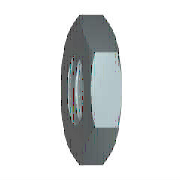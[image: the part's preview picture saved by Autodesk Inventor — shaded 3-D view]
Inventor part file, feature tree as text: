
AUTODESK INVENTOR PART (.ipt)
format: ipt  version: 2020 (Build 240168000, 168)  size: 167,424 bytes
history: native  units: mm (DEFAULTED — no unit token found)
features: sketch x3, chamfer x1, hole x1, other x1, plane x1
ambient origin geometry x7: Origin, YZ Plane, XZ Plane, X Axis, Y Axis, Z Axis, Center Point
bodies: Solid1 (feature_tree), Body (feature_tree)
feature tree (7):
  chamfer  "Chamfer1"  Angle=30.0deg  [1 undecoded]
  hole  "Thread"  [1 undecoded]
  other  "Work Axis1"
  plane  "Work Plane1"
  sketch  "Sketch1"  dims[d0=9.237604mm]
  sketch  "Sketch2"  dims[d1=2.7mm]
  sketch  "Sketch3"  dims[d2=0.0mm d3=30.0deg d4=30.0deg d5=6.9mm d6=6.9mm d7=90.0deg d25=4.134mm d26=6.0mm d27=4.0mm d28=2.0mm d29=14.3117mm d30=8.0mm d31=20.594885mm d8=0.433013mm d9=30.0deg d10=0.433013mm d11=30.0deg d13=0.0mm d14=0.0mm d39=0.0mm d40=0.433013mm d41=0.433013mm d42=0.0mm]
note: 2 required parameter values undecoded (feature->parameter linkage not recoverable at this tier; creation-order binding heuristic only, values carry confidence <= 0.55)
